# Revit family: Door_Barn_Maisy
name_source: partatom
category: Doors
units: mm (PartAtom-declared; Revit-internal decimal feet)

## family parameters
Always vertical = Yes
Classification Number = 23.30.10.17.11
Cut with Voids When Loaded = No
Host = Wall
Room Calculation Point = No
Shared = No

## types (1)
- Sherwin Williams Cumulos Cotton 2063-70
    Air Space Beneath Door = 0' - 0 7/16"
    Analytic Construction = <None>
    Assembly Code = C1020100
    Center Panel Material = Wood - Painted - Sherwin Williams Cumulos Cotton 2063-70
    Description = Renin Barn Door and Track - Stone Easy Slide Soft Close as Specified
    Door Design = Door_Barn-Panel_Renin_Maisy : Grooved Wood Panel
    Expected Lifespan (Years) = 0
    Fire Rating = As Specified
    Function = Interior
    Keynote = 08 00 00
    Maintenance Schedule (Months) = 0
    Manufacturer = Renin Corp
    Manufacturer Fax = 905-791-3813
    Manufacturer Website = https://www.renin.com
    Maximum Width = 0' - 0"
    Minimum Width = 0' - 0"
    Model = Maisy - Sherwin Williams Cumulos Cotton 2063-70
    Panel Height = 7' - 0"
    Panel Thickness = 0' - 1 3/8"
    Panel Width = 3' - 0"
    Product Data = http://www.arcat.com
    Sales Information = https://www.renin.com
    Sound Transmission Class (STC) = 0
    Thickness = 0' - 0"
    Track Width = 8' - 0"
    Type Comments = Confirm Opening Size Requirements
    URL = https://www.renin.com
    Wall Closure = By host
    Warranty Duration (Years) = 0
    longtrackmounts = Yes

## geometry (parser evidence)
native form markers: Blend x18, Sweep x9
no freeform markers — native parametric forms only
